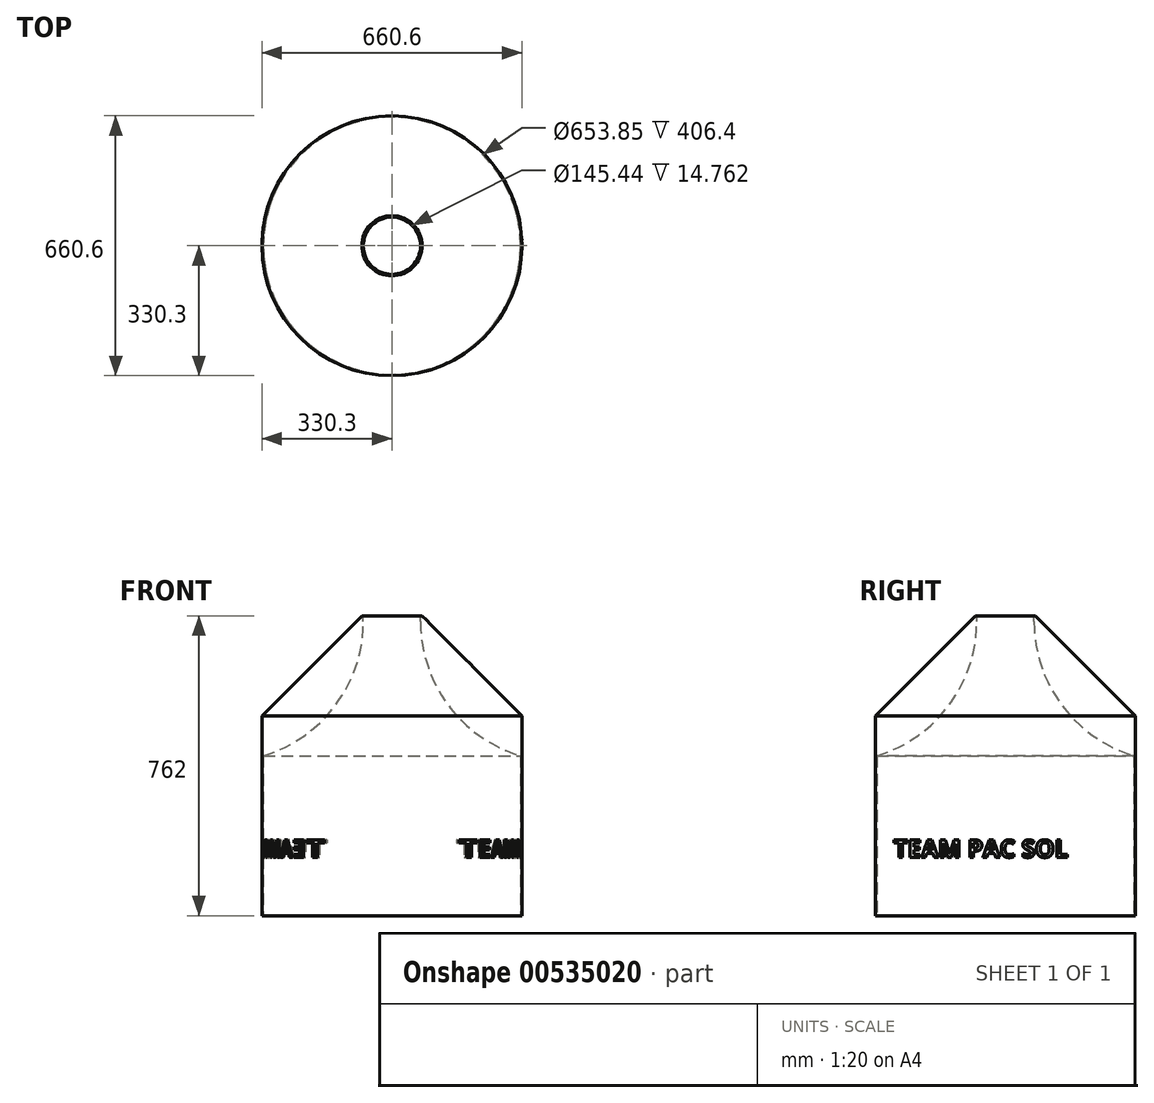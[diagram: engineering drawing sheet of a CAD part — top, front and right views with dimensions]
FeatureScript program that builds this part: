
annotation { "Feature Type Name" : "Feature", "Feature Type Description" : "" }
export const myFeature = defineFeature(function(context is Context, id is Id, definition is map)
    precondition{}
    {
        {
            var Q0;
            Q0=qCreatedBy(makeId("Top.planeOp"),FACE);
            var sketch = newSketch(context, id + "F0", { "sketchPlane" : qUnion([Q0])});
            skCircle(sketch, "E0", {"center": v(0, 0) * mm, "radius": 330.3 * mm});
            skSolve(sketch);
        }
        {
            var Q0;
            Q0=makeQuery(id+"F0.imprint","IMPRINT",FACE,{"disambiguationData":[TD([[makeQuery(id+"F0.imprint","IMPRINT",EDGE,{"derivedFrom":sQuery(id+"F0.wireOp",EDGE,"E0")}),1.0]])]});
            extrude(context, id + "F1", {"entities" : qUnion([Q0]), "depth" : 762 * mm, "offsetDistance" : 25.4 * mm});
        }
        {
            var Q0;
            Q0=makeQuery(id+"F1.opExtrude","CAP_FACE",FACE,{"disambiguationData":[OSD([sQuery(id+"F0.wireOp",EDGE,"E0")])],"isStart":false});
            var sketch = newSketch(context, id + "F2", { "sketchPlane" : qUnion([Q0])});
            skCircle(sketch, "E1", {"center": v(0, 0) * mm, "radius": 327.36 * mm});
            skSolve(sketch);
        }
        {
            var Q0;
            Q0=makeQuery(id+"F1.opExtrude","CAP_EDGE",EDGE,{"disambiguationData":[OSD([sQuery(id+"F0.wireOp",EDGE,"E0")])],"isStart":false});
            chamfer(context, id + "F3", {"entities" : qUnion([Q0]), "width" : 254 * mm, "tangentPropagation" : true});
        }
        {
            var Q0;
            Q0=makeQuery(id+"F2.imprint","IMPRINT",FACE,{"disambiguationData":[TD([[makeQuery(id+"F2.imprint","IMPRINT",EDGE,{"derivedFrom":sQuery(id+"F2.wireOp",EDGE,"E1")}),1.0]])]});
            var sketch = newSketch(context, id + "F4", { "sketchPlane" : qUnion([Q0])});
            skCircle(sketch, "E2", {"center": v(0, 0) * mm, "radius": 72.72 * mm});
            skSolve(sketch);
        }
        {
            var Q0;
            Q0 = qSketchRegion(id + "F4", true);
            extrude(context, id + "F5", {"entities" : qUnion([Q0]), "operationType" : NewBodyOperationType.REMOVE, "endBound" : BoundingType.THROUGH_ALL, "oppositeDirection" : true, "depth" : 25.4 * mm, "offsetDistance" : 25.4 * mm});
        }
        {
            var Q0;
            Q0=makeQuery(id+"F1.opExtrude","CAP_FACE",FACE,{"disambiguationData":[OSD([sQuery(id+"F0.wireOp",EDGE,"E0")])],"isStart":true});
            var sketch = newSketch(context, id + "F6", { "sketchPlane" : qUnion([Q0])});
            skCircle(sketch, "E3", {"center": v(0, 0) * mm, "radius": 326.92 * mm});
            skSolve(sketch);
        }
        {
            var Q0;
            Q0 = qSketchRegion(id + "F6", true);
            extrude(context, id + "F7", {"entities" : qUnion([Q0]), "operationType" : NewBodyOperationType.REMOVE, "oppositeDirection" : true, "depth" : 406.4 * mm, "offsetDistance" : 25.4 * mm});
        }
        {
            var Q0;
            Q0=makeQuery(id+"F7.boolean.opBoolean","INTERSECT",EDGE,{"derivedFrom":[makeQuery(id+"F5.boolean.opBoolean","COPY",FACE,{"derivedFrom":makeQuery(id+"F5.opExtrude","SWEPT_FACE",FACE,{"disambiguationData":[OSD([sQuery(id+"F4.wireOp",EDGE,"E2")])]})}),makeQuery(id+"F7.opExtrude","CAP_FACE",FACE,{"disambiguationData":[OSD([sQuery(id+"F6.wireOp",EDGE,"E3")])],"isStart":false})]});
            fillet(context, id + "F8", {"entities" : qUnion([Q0]), "radius" : 355.6 * mm, "tangentPropagation" : true, "allowEdgeOverflow" : false});
        }
        {
            var Q0;
            Q0=qCreatedBy(makeId("Right.planeOp"),FACE);
            var sketch = newSketch(context, id + "F9", { "sketchPlane" : qUnion([Q0])});
            skText(sketch, "E4", { "text": "TEAM PAC SOL", "fontName": "OpenSans-Bold.ttf"});
            const initialGuessF9  = {"E4": [-0.2839, 0.14822, 1, 0, 0.04461]};
            skSetInitialGuess(sketch, initialGuessF9);
            skSolve(sketch);
        }
        {
            var Q0;
            Q0 = qSketchRegion(id + "F9", true);
            extrude(context, id + "F10", {"entities" : qUnion([Q0]), "operationType" : NewBodyOperationType.REMOVE, "endBound" : BoundingType.SYMMETRIC, "oppositeDirection" : true, "depth" : 762 * mm, "offsetDistance" : 25.4 * mm});
        }
    });
